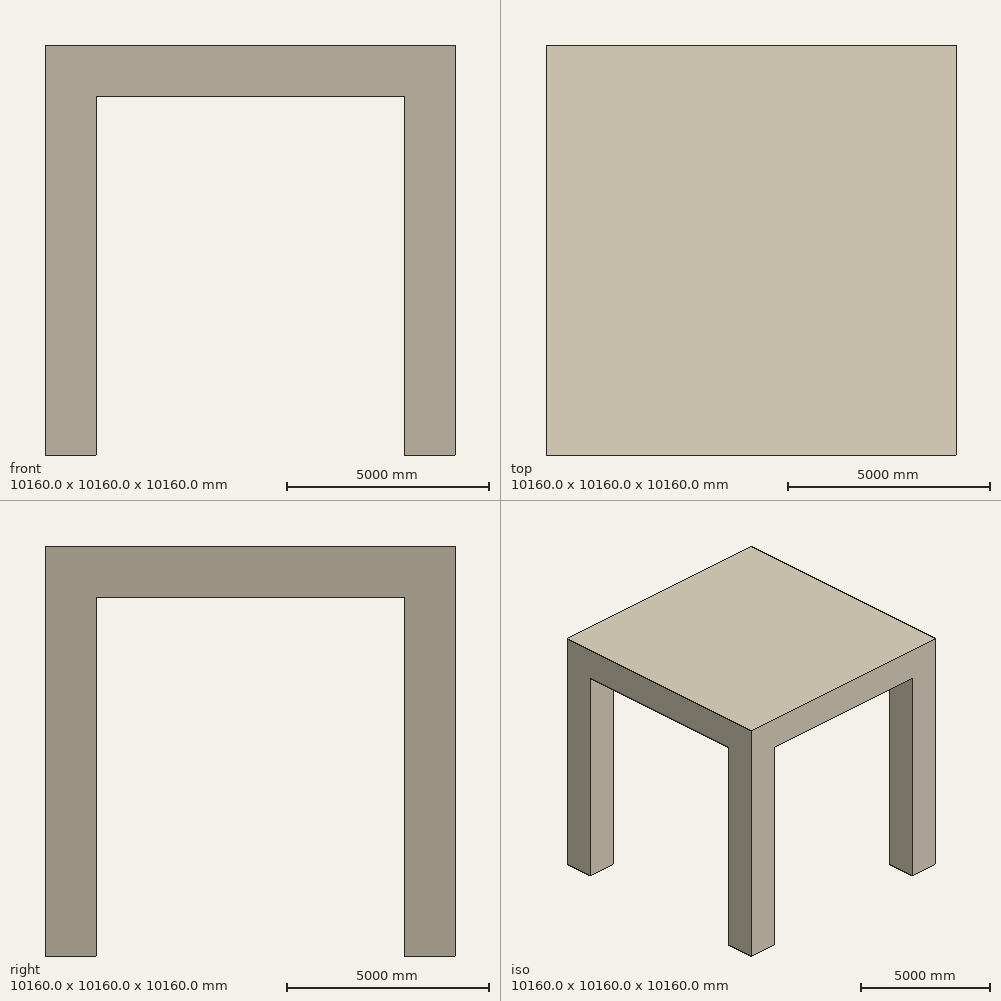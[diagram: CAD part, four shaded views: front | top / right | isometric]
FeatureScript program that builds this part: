
annotation { "Feature Type Name" : "Feature", "Feature Type Description" : "" }
export const myFeature = defineFeature(function(context is Context, id is Id, definition is map)
    precondition{}
    {
        {
            var Q0;
            Q0=qCreatedBy(makeId("Top.planeOp"),FACE);
            var sketch = newSketch(context, id + "F0", { "sketchPlane" : qUnion([Q0])});
            skLineSegment(sketch, "E0.bottom", {"start": v(-5064.43, 7289.67) * mm, "end": v(5095.57, 7289.67) * mm});
            skLineSegment(sketch, "E0.top", {"start": v(-5064.43, -2870.33) * mm, "end": v(5095.57, -2870.33) * mm});
            skLineSegment(sketch, "E0.left", {"start": v(-5064.43, 7289.67) * mm, "end": v(-5064.43, -2870.33) * mm});
            skLineSegment(sketch, "E0.right", {"start": v(5095.57, 7289.67) * mm, "end": v(5095.57, -2870.33) * mm});
            skPoint(sketch, "E0.middle", {"position": v(15.57, 2209.67) * mm});
            skSolve(sketch);
        }
        {
            var Q0;
            Q0=makeQuery(id+"F0.imprint","IMPRINT",FACE,{"disambiguationData":[TD([[makeQuery(id+"F0.imprint","IMPRINT",EDGE,{"derivedFrom":sQuery(id+"F0.wireOp",EDGE,"E0.bottom")}),-1.0]])]});
            extrude(context, id + "F1", {"entities" : qUnion([Q0]), "depth" : 10160 * mm, "offsetDistance" : 25.4 * mm});
        }
        {
            var Q0;
            Q0=makeQuery(id+"F1.opExtrude","SWEPT_FACE",FACE,{"disambiguationData":[OSD([sQuery(id+"F0.wireOp",EDGE,"E0.top")])]});
            var sketch = newSketch(context, id + "F2", { "sketchPlane" : qUnion([Q0])});
            skLineSegment(sketch, "E1.bottom", {"start": v(-3794.43, 0) * mm, "end": v(3825.57, 0) * mm});
            skLineSegment(sketch, "E1.top", {"start": v(-3794.43, 8890) * mm, "end": v(3825.57, 8890) * mm});
            skLineSegment(sketch, "E1.left", {"start": v(-3794.43, 0) * mm, "end": v(-3794.43, 8890) * mm});
            skLineSegment(sketch, "E1.right", {"start": v(3825.57, 0) * mm, "end": v(3825.57, 8890) * mm});
            skSolve(sketch);
        }
        {
            var Q0;
            Q0=makeQuery(id+"F2.imprint","IMPRINT",FACE,{"disambiguationData":[TD([[makeQuery(id+"F2.imprint","IMPRINT",EDGE,{"derivedFrom":sQuery(id+"F2.wireOp",EDGE,"E1.bottom")}),1.0]])]});
            extrude(context, id + "F3", {"entities" : qUnion([Q0]), "operationType" : NewBodyOperationType.REMOVE, "endBound" : BoundingType.THROUGH_ALL, "oppositeDirection" : true, "depth" : 25.4 * mm, "offsetDistance" : 25.4 * mm});
        }
        {
            var Q0;
            Q0=makeQuery(id+"F1.opExtrude","SWEPT_FACE",FACE,{"disambiguationData":[OSD([sQuery(id+"F0.wireOp",EDGE,"E0.left")])]});
            var sketch = newSketch(context, id + "F4", { "sketchPlane" : qUnion([Q0])});
            skLineSegment(sketch, "E2.bottom", {"start": v(-6019.67, 0) * mm, "end": v(1600.33, 0) * mm});
            skLineSegment(sketch, "E2.top", {"start": v(-6019.67, 8890) * mm, "end": v(1600.33, 8890) * mm});
            skLineSegment(sketch, "E2.left", {"start": v(-6019.67, 0) * mm, "end": v(-6019.67, 8890) * mm});
            skLineSegment(sketch, "E2.right", {"start": v(1600.33, 0) * mm, "end": v(1600.33, 8890) * mm});
            skSolve(sketch);
        }
        {
            var Q0;
            Q0=makeQuery(id+"F4.imprint","IMPRINT",FACE,{"disambiguationData":[TD([[makeQuery(id+"F4.imprint","IMPRINT",EDGE,{"derivedFrom":sQuery(id+"F4.wireOp",EDGE,"E2.bottom")}),1.0]])]});
            extrude(context, id + "F5", {"entities" : qUnion([Q0]), "operationType" : NewBodyOperationType.REMOVE, "endBound" : BoundingType.THROUGH_ALL, "oppositeDirection" : true, "depth" : 25.4 * mm, "offsetDistance" : 25.4 * mm});
        }
        {
            var Q0;
            Q0=makeQuery(id+"F1.opExtrude","CAP_FACE",FACE,{"disambiguationData":[OSD([sQuery(id+"F0.wireOp",EDGE,"E0.bottom"),sQuery(id+"F0.wireOp",EDGE,"E0.top"),sQuery(id+"F0.wireOp",EDGE,"E0.left"),sQuery(id+"F0.wireOp",EDGE,"E0.right")])],"isStart":false});
            cPlane(context, id + "F6", {"entities" : qUnion([Q0]), "cplaneType" : CPlaneType.OFFSET, "offset" : 0 * mm, "width" : 152.4 * mm, "height" : 152.4 * mm});
        }
        {
            var Q0;
            Q0=makeQuery(id+"F1.opExtrude","SWEPT_FACE",FACE,{"disambiguationData":[OSD([sQuery(id+"F0.wireOp",EDGE,"E0.top")])]});
            var Q1;
            Q1=makeQuery(id+"F1.opExtrude","CAP_VERTEX",VERTEX,{"disambiguationData":[OSD([sQuery(id+"F0.wireOp",EDGE,"E0.top"),sQuery(id+"F0.wireOp",EDGE,"E0.left")])],"isStart":false});
            cPlane(context, id + "F7", {"entities" : qUnion([Q0, Q1]), "cplaneType" : CPlaneType.PLANE_POINT, "offset" : 25.4 * mm, "width" : 152.4 * mm, "height" : 152.4 * mm});
        }
        {
            var Q0;
            Q0=qCreatedBy(id+"F7.planeOp",FACE);
            var sketch = newSketch(context, id + "F8", { "sketchPlane" : qUnion([Q0])});
            skLineSegment(sketch, "E3", {"start": v(-5063.81, 10160) * mm, "end": v(5142.53, 10160) * mm, "construction": true});
            skSolve(sketch);
        }
        {
            var Q0;
            Q0=qCreatedBy(id+"F7.planeOp",FACE);
            var Q1;
            Q1=sQuery(id+"F8.wireOp",EDGE,"E3");
            cPlane(context, id + "F9", {"entities" : qUnion([Q0, Q1]), "cplaneType" : CPlaneType.LINE_ANGLE, "offset" : 25.4 * mm, "angle" : 6 * degree, "width" : 152.4 * mm, "height" : 152.4 * mm});
        }
    });
